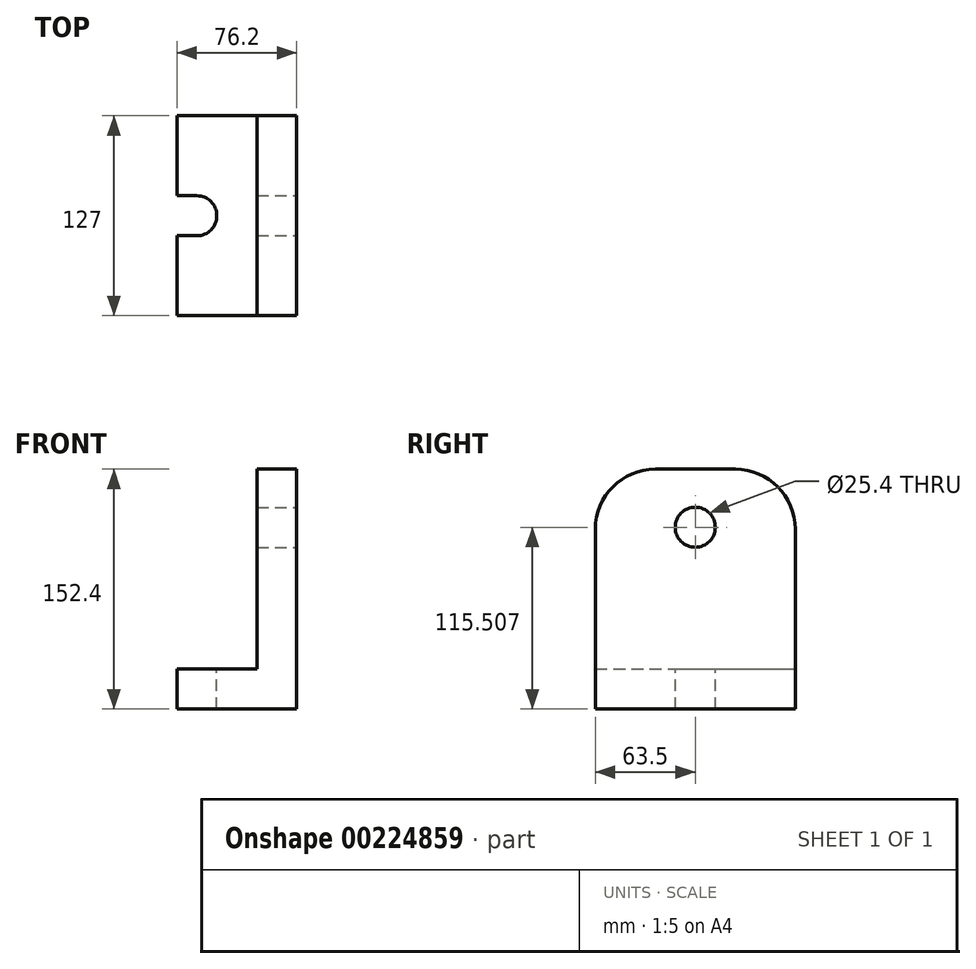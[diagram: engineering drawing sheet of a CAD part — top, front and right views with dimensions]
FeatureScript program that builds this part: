
annotation { "Feature Type Name" : "Feature", "Feature Type Description" : "" }
export const myFeature = defineFeature(function(context is Context, id is Id, definition is map)
    precondition{}
    {
        {
            var Q0;
            Q0=qCreatedBy(makeId("Front.planeOp"),FACE);
            var sketch = newSketch(context, id + "F0", { "sketchPlane" : qUnion([Q0])});
            skLineSegment(sketch, "E0", {"start": v(0, 0) * mm, "end": v(0, 152.4) * mm});
            skLineSegment(sketch, "E1", {"start": v(0, 0) * mm, "end": v(-76.2, 0) * mm});
            skLineSegment(sketch, "E2", {"start": v(-76.2, 0) * mm, "end": v(-76.2, 25.4) * mm});
            skLineSegment(sketch, "E3", {"start": v(-76.2, 25.4) * mm, "end": v(-25.4, 25.4) * mm});
            skLineSegment(sketch, "E4", {"start": v(-25.4, 25.4) * mm, "end": v(-25.4, 152.4) * mm});
            skLineSegment(sketch, "E5", {"start": v(-25.4, 152.4) * mm, "end": v(0, 152.4) * mm});
            skSolve(sketch);
        }
        {
            var Q0;
            Q0 = qSketchRegion(id + "F0", true);
            extrude(context, id + "F1", {"entities" : qUnion([Q0]), "endBound" : BoundingType.SYMMETRIC, "depth" : 127 * mm});
        }
        {
            var Q0;
            Q0=makeQuery(id+"F1.opExtrude","SWEPT_FACE",FACE,{"disambiguationData":[OSD([sQuery(id+"F0.wireOp",EDGE,"E0")])]});
            var sketch = newSketch(context, id + "F2", { "sketchPlane" : qUnion([Q0])});
            skLineSegment(sketch, "E6", {"start": v(0, 0) * mm, "end": v(0, 152.4) * mm, "construction": true});
            skCircle(sketch, "E7", {"center": v(0, 115.5) * mm, "radius": 12.7 * mm});
            skSolve(sketch);
        }
        {
            var Q0;
            Q0=makeQuery(id+"F2.imprint","IMPRINT",FACE,{"disambiguationData":[TD([[makeQuery(id+"F2.imprint","IMPRINT",EDGE,{"derivedFrom":sQuery(id+"F2.wireOp",EDGE,"E7")}),1.0]])]});
            extrude(context, id + "F3", {"entities" : qUnion([Q0]), "operationType" : NewBodyOperationType.REMOVE, "oppositeDirection" : true, "depth" : 25.4 * mm});
        }
        {
            var Q0;
            Q0=makeQuery(id+"F1.opExtrude","SWEPT_FACE",FACE,{"disambiguationData":[OSD([sQuery(id+"F0.wireOp",EDGE,"E3")])]});
            var sketch = newSketch(context, id + "F4", { "sketchPlane" : qUnion([Q0])});
            skLineSegment(sketch, "E8.bottom", {"start": v(-63.5, -12.7) * mm, "end": v(-76.2, -12.7) * mm});
            skLineSegment(sketch, "E8.top", {"start": v(-63.5, 12.7) * mm, "end": v(-76.2, 12.7) * mm});
            skLineSegment(sketch, "E8.left", {"start": v(-63.5, -12.7) * mm, "end": v(-63.5, 12.7) * mm});
            skLineSegment(sketch, "E8.right", {"start": v(-76.2, -12.7) * mm, "end": v(-76.2, 12.7) * mm});
            skPoint(sketch, "E8.middle", {"position": v(-69.84, 0) * mm});
            skArc(sketch, "E9", {"start": v(-63.5, -12.7) * mm, "mid": v(-50.8, 0) * mm, "end": v(-63.5, 12.7) * mm});
            skSolve(sketch);
        }
        {
            var Q0;
            Q0 = qSketchRegion(id + "F4", true);
            extrude(context, id + "F5", {"entities" : qUnion([Q0]), "operationType" : NewBodyOperationType.REMOVE, "endBound" : BoundingType.THROUGH_ALL, "oppositeDirection" : true, "depth" : 25.4 * mm});
        }
        {
            var Q0;
            Q0=makeQuery(id+"F1.opExtrude","CAP_EDGE",EDGE,{"disambiguationData":[OSD([sQuery(id+"F0.wireOp",EDGE,"E5")])],"isStart":true});
            var Q1;
            Q1=makeQuery(id+"F1.opExtrude","CAP_EDGE",EDGE,{"disambiguationData":[OSD([sQuery(id+"F0.wireOp",EDGE,"E5")])],"isStart":false});
            fillet(context, id + "F6", {"entities" : qUnion([Q0, Q1]), "radius" : 38.1 * mm, "tangentPropagation" : true, "allowEdgeOverflow" : false});
        }
        {
            var Q0;
            Q0=qCreatedBy(makeId("Front.planeOp"),FACE);
            cPlane(context, id + "F7", {"entities" : qUnion([Q0]), "cplaneType" : CPlaneType.OFFSET, "offset" : 44.45 * mm, "width" : 152.4 * mm, "height" : 152.4 * mm});
        }
    });
